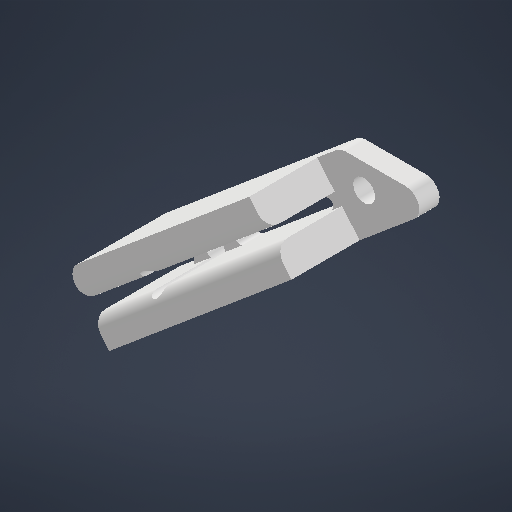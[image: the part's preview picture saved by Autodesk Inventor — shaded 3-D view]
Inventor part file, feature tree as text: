
AUTODESK INVENTOR PART (.ipt)
format: ipt  version: 2025 (Build 290162000, 162)  size: 289,280 bytes
history: native  units: mm
features: other x3, extrude x2, fillet x2, sketch x2, reference x1, projected_geometry x1
ambient origin geometry x8: Origin, YZ Plane, XZ Plane, XY Plane, X Axis, Y Axis, Z Axis, Center Point
bodies: Solid1 (feature_tree)
feature tree (11):
  extrude  "Extrusion1"  Depth=2.0mm TaperAngle=0.0deg
  fillet  "Fillet1"  Radius=2.0mm
  extrude  "Extrusion2"  Depth=10.0mm TaperAngle=0.0deg
  fillet  "Fillet2"  Radius=2.0mm
  sketch  "Sketch1"  dims[d0=35.0mm d1=3.0mm d2=0.0mm d3=2.0mm]
  reference  "Reference1"
  sketch  "Sketch2"  dims[d4=35.0mm d5=10.0mm d6=0.0mm d7=2.0mm]
  projected_geometry  "Projected Loop1"
  other  "<userpath> 7 was better\GitHub\ReplicatorPlusConversion\CAD\Inventor\Electronics.iam"
  other  "Electronics.iam"
  other  "rpi-mount:1"
